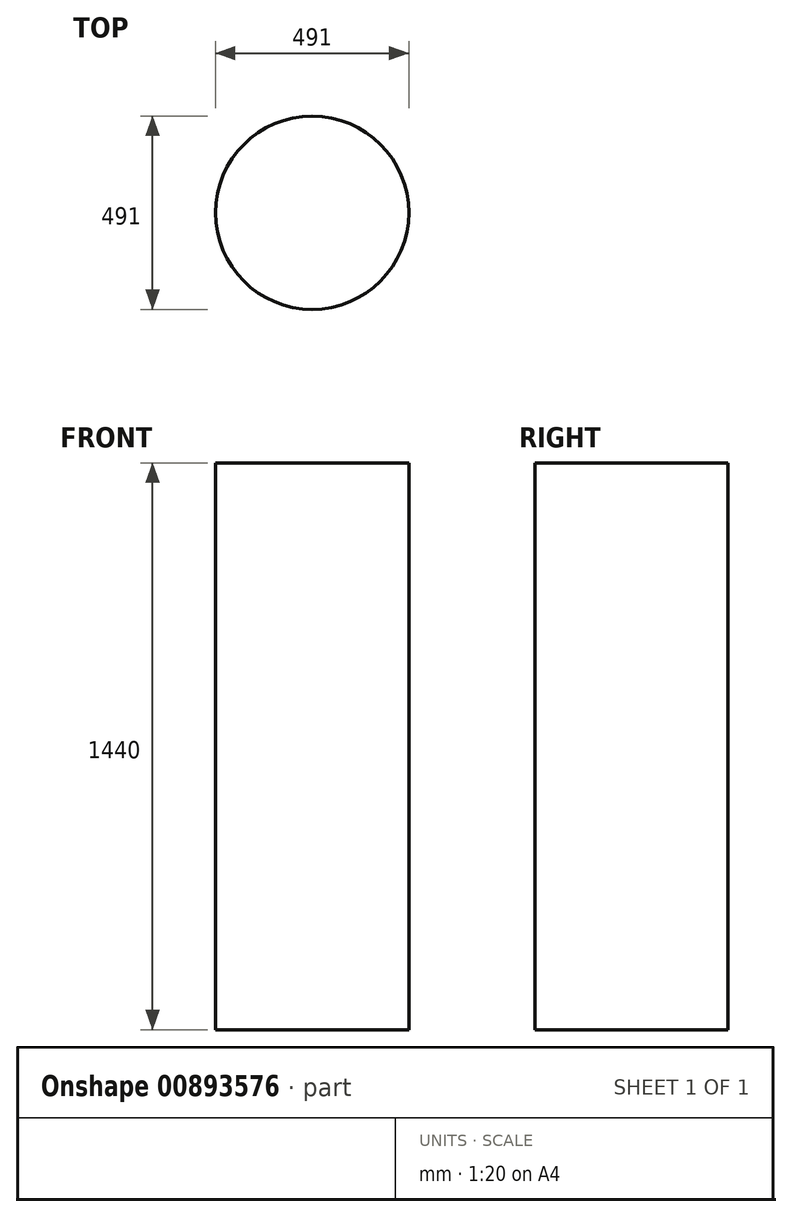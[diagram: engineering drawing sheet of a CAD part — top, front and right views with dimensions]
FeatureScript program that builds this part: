
annotation { "Feature Type Name" : "Feature", "Feature Type Description" : "" }
export const myFeature = defineFeature(function(context is Context, id is Id, definition is map)
    precondition{}
    {
        {
            var Q0;
            Q0=qCreatedBy(makeId("Top.planeOp"),FACE);
            var sketch = newSketch(context, id + "F0", { "sketchPlane" : qUnion([Q0])});
            skCircle(sketch, "E0", {"center": v(0, 0) * mm, "radius": 245.5 * mm});
            skSolve(sketch);
        }
        {
            var Q0;
            Q0 = qSketchRegion(id + "F0", true);
            extrude(context, id + "F1", {"entities" : qUnion([Q0]), "depth" : 1440 * mm, "offsetDistance" : 25 * mm});
        }
    });
